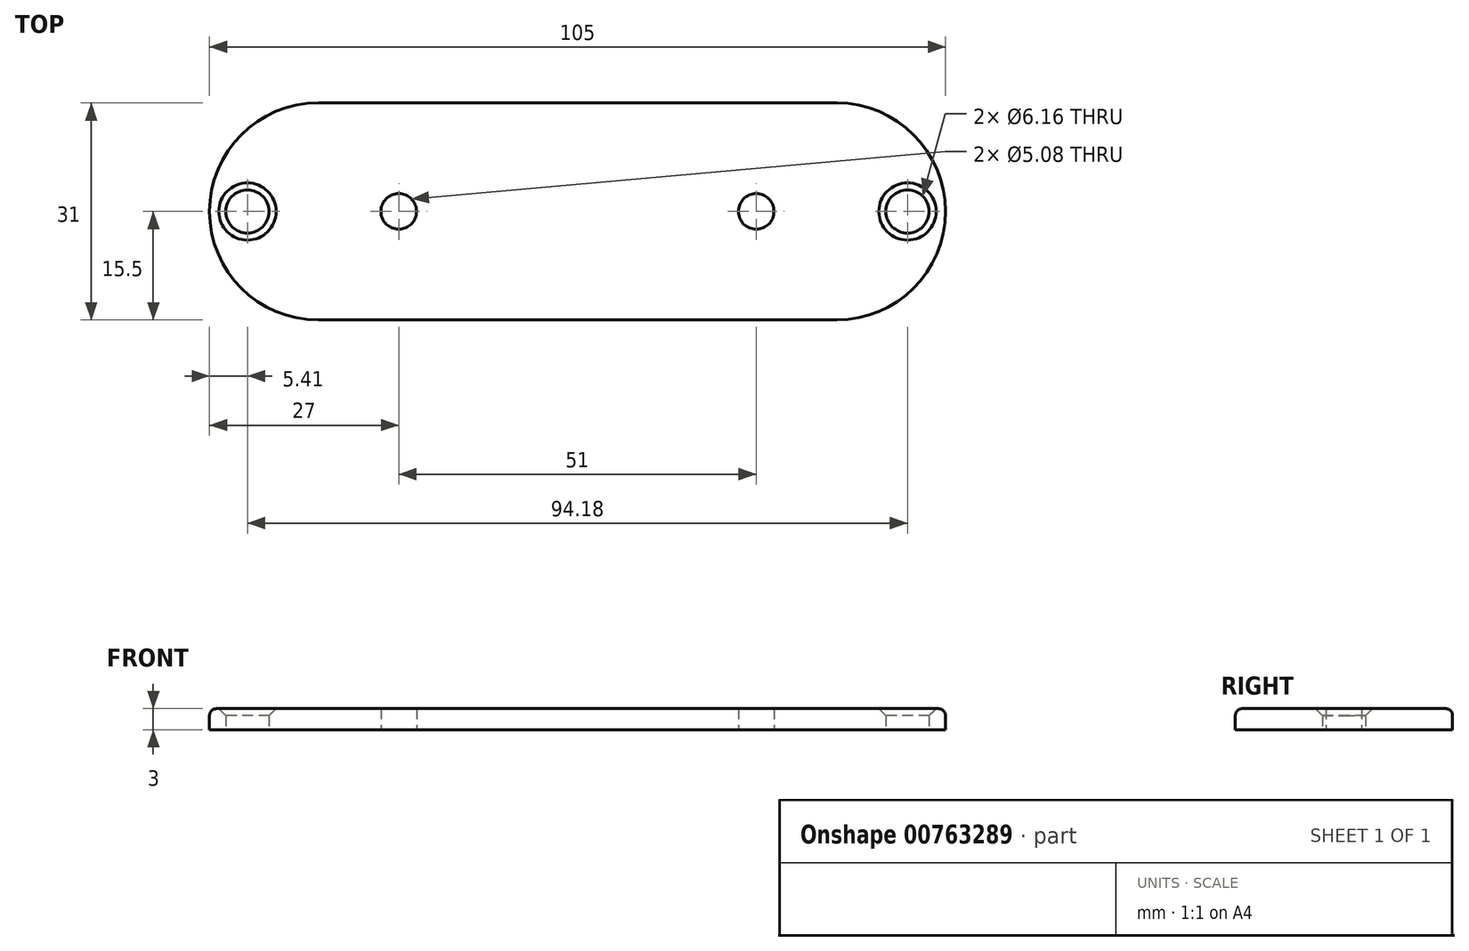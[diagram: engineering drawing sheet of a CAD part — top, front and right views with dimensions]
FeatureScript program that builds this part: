
annotation { "Feature Type Name" : "Feature", "Feature Type Description" : "" }
export const myFeature = defineFeature(function(context is Context, id is Id, definition is map)
    precondition{}
    {
        {
            var Q0;
            Q0=qCreatedBy(makeId("Top.planeOp"),FACE);
            var sketch = newSketch(context, id + "F0", { "sketchPlane" : qUnion([Q0])});
            skLineSegment(sketch, "E0.bottom", {"start": v(-37, 15.5) * mm, "end": v(37, 15.5) * mm});
            skLineSegment(sketch, "E0.top", {"start": v(-37, -15.5) * mm, "end": v(37, -15.5) * mm});
            skPoint(sketch, "E0.middle", {"position": v(0, 0) * mm});
            skArc(sketch, "E1", {"start": v(-37, 15.5) * mm, "mid": v(-52.5, 0) * mm, "end": v(-37, -15.5) * mm});
            skArc(sketch, "E2", {"start": v(37, -15.5) * mm, "mid": v(52.5, 0) * mm, "end": v(37, 15.5) * mm});
            skCircle(sketch, "E3", {"center": v(-47.1, 0) * mm, "radius": 3.08 * mm});
            skCircle(sketch, "E4", {"center": v(-25.5, 0) * mm, "radius": 2.54 * mm});
            skLineSegment(sketch, "E5", {"start": v(0, 0) * mm, "end": v(0, 15.5) * mm, "construction": true});
            skLineSegment(sketch, "E6", {"start": v(0, 15.5) * mm, "end": v(0, 0) * mm, "construction": true});
            skLineSegment(sketch, "E7", {"start": v(0, 0) * mm, "end": v(0, -15.5) * mm, "construction": true});
            skCircle(sketch, "E8.MirrorC", {"center": v(25.5, 0) * mm, "radius": 2.54 * mm});
            skCircle(sketch, "E9.MirrorC", {"center": v(47.1, 0) * mm, "radius": 3.08 * mm});
            skSolve(sketch);
        }
        {
            var Q0;
            Q0 = qSketchRegion(id + "F0", true);
            extrude(context, id + "F1", {"entities" : qUnion([Q0]), "depth" : 3 * mm, "offsetDistance" : 25 * mm});
        }
        {
            var Q0;
            Q0=makeQuery(id+"F1.opExtrude","CAP_EDGE",EDGE,{"disambiguationData":[OSD([sQuery(id+"F0.wireOp",EDGE,"E1")])],"isStart":false});
            fillet(context, id + "F2", {"entities" : qUnion([Q0]), "radius" : 1 * mm, "tangentPropagation" : true, "allowEdgeOverflow" : false});
        }
        {
            var Q0;
            Q0=makeQuery(id+"F1.opExtrude","CAP_EDGE",EDGE,{"disambiguationData":[OSD([sQuery(id+"F0.wireOp",EDGE,"E3")])],"isStart":false});
            var Q1;
            Q1=makeQuery(id+"F1.opExtrude","CAP_EDGE",EDGE,{"disambiguationData":[OSD([sQuery(id+"F0.wireOp",EDGE,"E9.MirrorC")])],"isStart":false});
            chamfer(context, id + "F3", {"entities" : qUnion([Q0, Q1]), "width" : 1 * mm, "tangentPropagation" : true});
        }
    });
